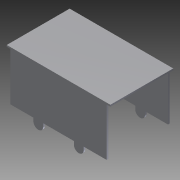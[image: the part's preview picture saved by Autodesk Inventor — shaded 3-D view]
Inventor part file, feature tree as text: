
AUTODESK INVENTOR PART (.ipt)
format: ipt  version: 2011 SP1 (Build 150282100, 282)  size: 109,568 bytes
history: native  units: in
note: dims shown in document units (in); Inventor stores cm internally (conversion verified against a paired STEP export)
features: other x7, extrude x3, sketch x3
ambient origin geometry x8: Origin, YZ Plane, XZ Plane, XY Plane, X Axis, Y Axis, Z Axis, Center Point
bodies: Solid1 (feature_tree)
feature tree (13):
  extrude  "Extrusion1"  Depth=0.008in TaperAngle=0.0deg
  extrude  "Extrusion2"  [1 undecoded]
  extrude  "Extrusion3"  [1 undecoded]
  other  "shroud_to_body_XY"
  other  "shroud_to_body_YZ"
  other  "shroud_to_body_ZX"
  other  "shroud_to_body_X"
  other  "shroud_to_body_Y"
  other  "shroud_to_body_Z"
  other  "shroud_to_body_Center"
  sketch  "Sketch_1"  dims[d0=0.008in d1=0.0in d2=0.008in d3=0.0in]
  sketch  "Sketch_2"  dims[d4=0.008in d5=0.0in]
  sketch  "Sketch_3"
note: 2 required parameter values undecoded (feature->parameter linkage not recoverable at this tier; creation-order binding heuristic only, values carry confidence <= 0.55)
